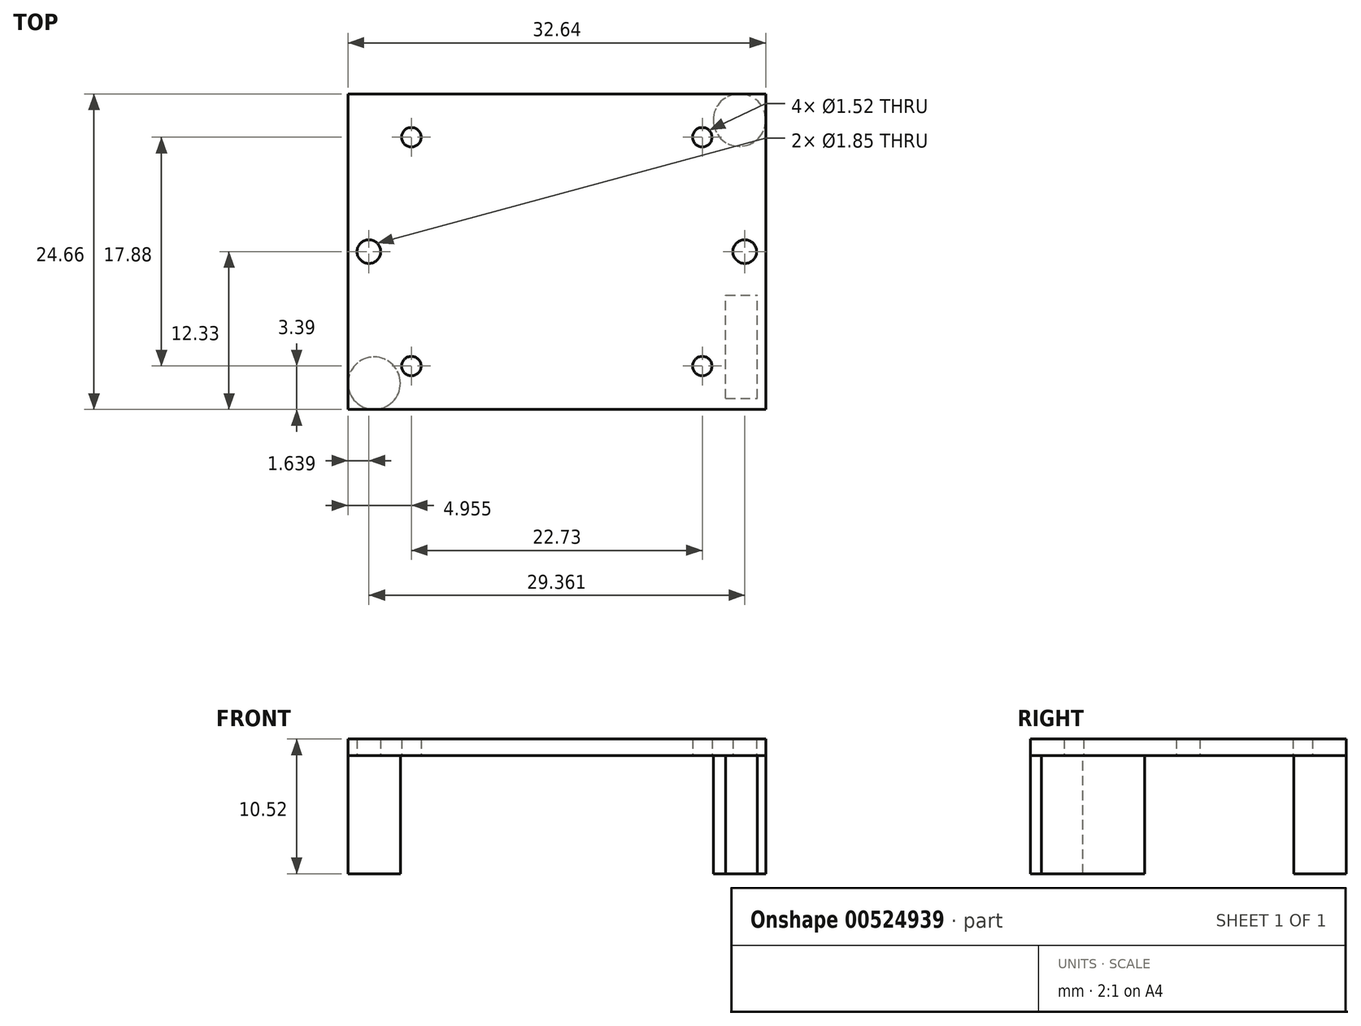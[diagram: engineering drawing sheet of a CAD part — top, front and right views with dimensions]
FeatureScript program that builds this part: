
annotation { "Feature Type Name" : "Feature", "Feature Type Description" : "" }
export const myFeature = defineFeature(function(context is Context, id is Id, definition is map)
    precondition{}
    {
        {
            var Q0;
            Q0=qCreatedBy(makeId("Top.planeOp"),FACE);
            var sketch = newSketch(context, id + "F0", { "sketchPlane" : qUnion([Q0])});
            skPoint(sketch, "E0.middle", {"position": v(0, 0) * mm});
            skCircle(sketch, "E1", {"center": v(-11.37, -8.94) * mm, "radius": 0.76 * mm});
            skCircle(sketch, "E2", {"center": v(11.37, -8.94) * mm, "radius": 0.76 * mm});
            skCircle(sketch, "E3", {"center": v(-11.37, 8.94) * mm, "radius": 0.76 * mm});
            skCircle(sketch, "E4", {"center": v(11.37, 8.94) * mm, "radius": 0.76 * mm});
            skLineSegment(sketch, "E5", {"start": v(-28.2, 0) * mm, "end": v(25.53, 0) * mm, "construction": true});
            skCircle(sketch, "E6", {"center": v(-14.68, 0) * mm, "radius": 0.93 * mm});
            skCircle(sketch, "E7", {"center": v(14.68, 0) * mm, "radius": 0.93 * mm});
            skLineSegment(sketch, "E8.bottom", {"start": v(16.32, 12.33) * mm, "end": v(-16.32, 12.33) * mm});
            skLineSegment(sketch, "E8.top", {"start": v(16.32, -12.33) * mm, "end": v(-16.32, -12.33) * mm});
            skLineSegment(sketch, "E8.left", {"start": v(16.32, 12.33) * mm, "end": v(16.32, -12.33) * mm});
            skLineSegment(sketch, "E8.right", {"start": v(-16.32, 12.33) * mm, "end": v(-16.32, -12.33) * mm});
            skSolve(sketch);
        }
        {
            var Q0;
            Q0=makeQuery(id+"F0.imprint","IMPRINT",FACE,{"disambiguationData":[TD([[makeQuery(id+"F0.imprint","IMPRINT",EDGE,{"derivedFrom":sQuery(id+"F0.wireOp",EDGE,"E1")}),-1.0]])]});
            extrude(context, id + "F1", {"entities" : qUnion([Q0]), "depth" : 1.3 * mm, "offsetDistance" : 25 * mm});
        }
        {
            var Q0;
            Q0=makeQuery(id+"F1.opExtrude","CAP_FACE",FACE,{"disambiguationData":[OSD([sQuery(id+"F0.wireOp",EDGE,"E1"),sQuery(id+"F0.wireOp",EDGE,"E2"),sQuery(id+"F0.wireOp",EDGE,"E3"),sQuery(id+"F0.wireOp",EDGE,"E4"),sQuery(id+"F0.wireOp",EDGE,"E6"),sQuery(id+"F0.wireOp",EDGE,"E7"),sQuery(id+"F0.wireOp",EDGE,"E8.bottom"),sQuery(id+"F0.wireOp",EDGE,"E8.top"),sQuery(id+"F0.wireOp",EDGE,"E8.left"),sQuery(id+"F0.wireOp",EDGE,"E8.right")])],"isStart":true});
            cPlane(context, id + "F2", {"entities" : qUnion([Q0]), "cplaneType" : CPlaneType.OFFSET, "offset" : 0 * mm, "width" : 150 * mm, "height" : 150 * mm});
        }
        {
            var Q0;
            Q0=qCreatedBy(id+"F2.planeOp",FACE);
            var sketch = newSketch(context, id + "F3", { "sketchPlane" : qUnion([Q0])});
            skCircle(sketch, "E9", {"center": v(-14.27, 10.28) * mm, "radius": 2.05 * mm});
            skCircle(sketch, "E10.MirrorC", {"center": v(-14.27, -10.28) * mm, "radius": 2.05 * mm});
            skCircle(sketch, "E11.MirrorC", {"center": v(14.27, -10.28) * mm, "radius": 2.05 * mm});
            skLineSegment(sketch, "E12.bottom", {"start": v(13.2, 11.48) * mm, "end": v(15.67, 11.48) * mm});
            skLineSegment(sketch, "E12.top", {"start": v(13.2, 3.4) * mm, "end": v(15.67, 3.4) * mm});
            skLineSegment(sketch, "E12.left", {"start": v(13.2, 11.48) * mm, "end": v(13.2, 3.4) * mm});
            skLineSegment(sketch, "E12.right", {"start": v(15.67, 11.48) * mm, "end": v(15.67, 3.4) * mm});
            skSolve(sketch);
        }
        {
            var Q0;
            Q0=makeQuery(id+"F3.imprint","IMPRINT",FACE,{"disambiguationData":[TD([[makeQuery(id+"F3.imprint","IMPRINT",EDGE,{"derivedFrom":sQuery(id+"F3.wireOp",EDGE,"E9")}),1.0]])]});
            var Q1;
            Q1=makeQuery(id+"F3.imprint","IMPRINT",FACE,{"disambiguationData":[TD([[makeQuery(id+"F3.imprint","IMPRINT",EDGE,{"derivedFrom":sQuery(id+"F3.wireOp",EDGE,"E10.MirrorC")}),-1.0]])]});
            var Q2;
            Q2=makeQuery(id+"F3.imprint","IMPRINT",FACE,{"disambiguationData":[TD([[makeQuery(id+"F3.imprint","IMPRINT",EDGE,{"derivedFrom":sQuery(id+"F3.wireOp",EDGE,"E11.MirrorC")}),1.0]])]});
            var Q3;
            Q3=makeQuery(id+"F3.imprint","IMPRINT",FACE,{"disambiguationData":[TD([[makeQuery(id+"F3.imprint","IMPRINT",EDGE,{"derivedFrom":sQuery(id+"F3.wireOp",EDGE,"E12.bottom")}),-1.0]])]});
            extrude(context, id + "F4", {"entities" : qUnion([Q0, Q1, Q2, Q3]), "operationType" : NewBodyOperationType.ADD, "depth" : 9.22 * mm, "offsetDistance" : 25 * mm});
        }
    });
